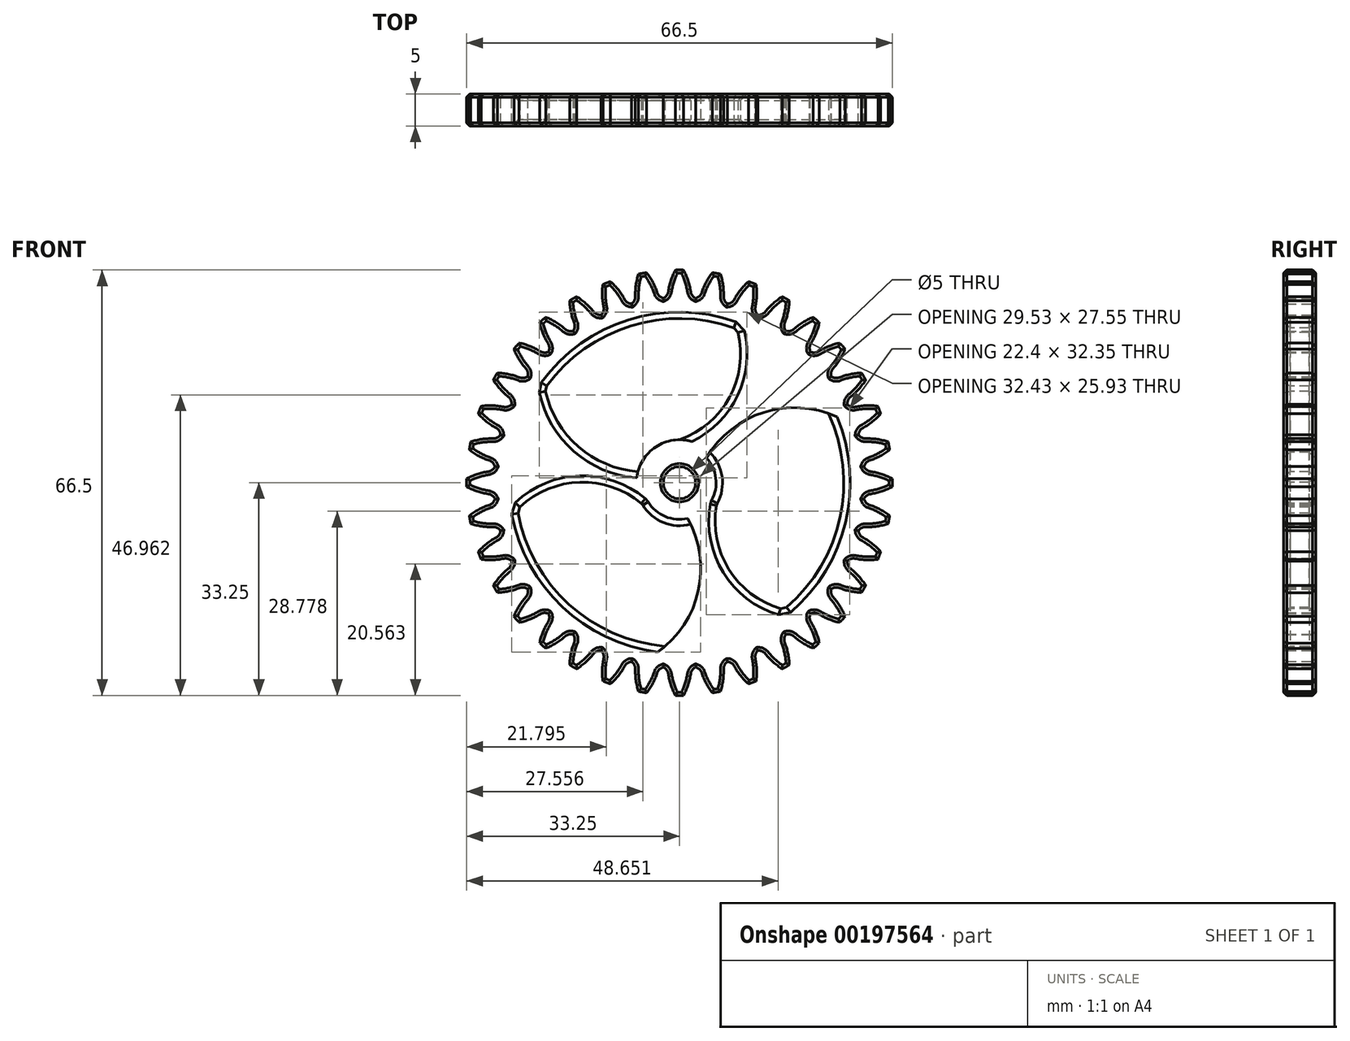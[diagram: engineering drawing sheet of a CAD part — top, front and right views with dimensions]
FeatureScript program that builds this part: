
annotation { "Feature Type Name" : "Feature", "Feature Type Description" : "" }
export const myFeature = defineFeature(function(context is Context, id is Id, definition is map)
    precondition{}
    {
        {
            var Q0;
            Q0=qCreatedBy(makeId("Front.planeOp"),FACE);
            var sketch = newSketch(context, id + "F0", { "sketchPlane" : qUnion([Q0])});
            skCircle(sketch, "E0", {"center": v(0, 0) * mm, "radius": 31.5 * mm, "construction": true});
            skCircle(sketch, "E1", {"center": v(0, 0) * mm, "radius": 29.6 * mm, "construction": true});
            skLineSegment(sketch, "E2", {"start": v(0, 0) * mm, "end": v(12.73, 40.38) * mm, "construction": true});
            skLineSegment(sketch, "E3", {"start": v(0, 0) * mm, "end": v(-1.92, 44) * mm, "construction": true});
            skLineSegment(sketch, "E4", {"start": v(0, 0) * mm, "end": v(0, 61.73) * mm, "construction": true});
            skArc(sketch, "E5", {"start": v(-0.64, 33.24) * mm, "mid": v(-1.33, 31.6) * mm, "end": v(-1.75, 29.87) * mm});
            skArc(sketch, "E6", {"start": v(0, 33.25) * mm, "mid": v(-0.32, 33.25) * mm, "end": v(-0.64, 33.24) * mm});
            skArc(sketch, "E7.MirrorCS", {"start": v(0, 33.25) * mm, "mid": v(0.32, 33.25) * mm, "end": v(0.64, 33.24) * mm});
            skArc(sketch, "E8.MirrorCS", {"start": v(0.64, 33.24) * mm, "mid": v(1.33, 31.6) * mm, "end": v(1.75, 29.87) * mm});
            skArc(sketch, "E9.filletArc", {"start": v(1.75, 29.87) * mm, "mid": v(2, 29.26) * mm, "end": v(2.52, 28.84) * mm});
            skArc(sketch, "E10.MirrorCS", {"start": v(-1.75, 29.87) * mm, "mid": v(-2, 29.26) * mm, "end": v(-2.52, 28.84) * mm});
            skArc(sketch, "E11.1.0", {"start": v(-5.77, 32.74) * mm, "mid": v(-6.09, 32.69) * mm, "end": v(-6.4, 32.63) * mm});
            skArc(sketch, "E11.1.1", {"start": v(-5.77, 32.74) * mm, "mid": v(-5.46, 32.8) * mm, "end": v(-5.15, 32.85) * mm});
            skArc(sketch, "E11.1.2", {"start": v(-5.15, 32.85) * mm, "mid": v(-4.18, 31.36) * mm, "end": v(-3.47, 29.72) * mm});
            skArc(sketch, "E11.1.3", {"start": v(-6.9, 29.12) * mm, "mid": v(-7.05, 28.47) * mm, "end": v(-7.5, 27.97) * mm});
            skArc(sketch, "E11.1.4", {"start": v(-6.4, 32.63) * mm, "mid": v(-6.8, 30.9) * mm, "end": v(-6.9, 29.12) * mm});
            skArc(sketch, "E11.1.5", {"start": v(-3.47, 29.72) * mm, "mid": v(-3.1, 29.16) * mm, "end": v(-2.52, 28.84) * mm});
            skArc(sketch, "E11.2.0", {"start": v(-11.37, 31.24) * mm, "mid": v(-11.67, 31.13) * mm, "end": v(-11.97, 31.02) * mm});
            skArc(sketch, "E11.2.1", {"start": v(-11.37, 31.24) * mm, "mid": v(-11.07, 31.35) * mm, "end": v(-10.77, 31.46) * mm});
            skArc(sketch, "E11.2.2", {"start": v(-10.77, 31.46) * mm, "mid": v(-9.56, 30.15) * mm, "end": v(-8.58, 28.67) * mm});
            skArc(sketch, "E11.2.3", {"start": v(-11.86, 27.48) * mm, "mid": v(-11.9, 26.8) * mm, "end": v(-12.24, 26.24) * mm});
            skArc(sketch, "E11.2.4", {"start": v(-11.97, 31.02) * mm, "mid": v(-12.06, 29.24) * mm, "end": v(-11.86, 27.48) * mm});
            skArc(sketch, "E11.2.5", {"start": v(-8.58, 28.67) * mm, "mid": v(-8.12, 28.18) * mm, "end": v(-7.5, 27.97) * mm});
            skArc(sketch, "E11.3.0", {"start": v(-16.63, 28.8) * mm, "mid": v(-16.9, 28.63) * mm, "end": v(-17.17, 28.47) * mm});
            skArc(sketch, "E11.3.1", {"start": v(-16.62, 28.8) * mm, "mid": v(-16.35, 28.95) * mm, "end": v(-16.07, 29.1) * mm});
            skArc(sketch, "E11.3.2", {"start": v(-16.07, 29.1) * mm, "mid": v(-14.65, 28.04) * mm, "end": v(-13.43, 26.74) * mm});
            skArc(sketch, "E11.3.3", {"start": v(-16.45, 25) * mm, "mid": v(-16.37, 24.34) * mm, "end": v(-16.6, 23.72) * mm});
            skArc(sketch, "E11.3.4", {"start": v(-17.17, 28.47) * mm, "mid": v(-16.95, 26.7) * mm, "end": v(-16.45, 25) * mm});
            skArc(sketch, "E11.3.5", {"start": v(-13.43, 26.74) * mm, "mid": v(-12.9, 26.34) * mm, "end": v(-12.24, 26.24) * mm});
            skArc(sketch, "E11.4.0", {"start": v(-21.37, 25.47) * mm, "mid": v(-21.62, 25.27) * mm, "end": v(-21.86, 25.06) * mm});
            skArc(sketch, "E11.4.1", {"start": v(-21.37, 25.47) * mm, "mid": v(-21.13, 25.67) * mm, "end": v(-20.88, 25.88) * mm});
            skArc(sketch, "E11.4.2", {"start": v(-20.88, 25.88) * mm, "mid": v(-19.3, 25.07) * mm, "end": v(-17.87, 24) * mm});
            skArc(sketch, "E11.4.3", {"start": v(-20.54, 21.76) * mm, "mid": v(-20.34, 21.13) * mm, "end": v(-20.47, 20.47) * mm});
            skArc(sketch, "E11.4.4", {"start": v(-21.86, 25.06) * mm, "mid": v(-21.33, 23.36) * mm, "end": v(-20.54, 21.76) * mm});
            skArc(sketch, "E11.4.5", {"start": v(-17.87, 24) * mm, "mid": v(-17.27, 23.7) * mm, "end": v(-16.6, 23.72) * mm});
            skArc(sketch, "E11.5.0", {"start": v(-25.47, 21.37) * mm, "mid": v(-25.67, 21.13) * mm, "end": v(-25.88, 20.88) * mm});
            skArc(sketch, "E11.5.1", {"start": v(-25.47, 21.37) * mm, "mid": v(-25.27, 21.62) * mm, "end": v(-25.06, 21.86) * mm});
            skArc(sketch, "E11.5.2", {"start": v(-25.06, 21.86) * mm, "mid": v(-23.36, 21.33) * mm, "end": v(-21.76, 20.54) * mm});
            skArc(sketch, "E11.5.3", {"start": v(-24, 17.87) * mm, "mid": v(-23.7, 17.27) * mm, "end": v(-23.72, 16.6) * mm});
            skArc(sketch, "E11.5.4", {"start": v(-25.88, 20.88) * mm, "mid": v(-25.07, 19.3) * mm, "end": v(-24, 17.87) * mm});
            skArc(sketch, "E11.5.5", {"start": v(-21.76, 20.54) * mm, "mid": v(-21.13, 20.34) * mm, "end": v(-20.47, 20.47) * mm});
            skArc(sketch, "E11.6.0", {"start": v(-28.8, 16.62) * mm, "mid": v(-28.95, 16.35) * mm, "end": v(-29.1, 16.07) * mm});
            skArc(sketch, "E11.6.1", {"start": v(-28.8, 16.63) * mm, "mid": v(-28.63, 16.9) * mm, "end": v(-28.47, 17.17) * mm});
            skArc(sketch, "E11.6.2", {"start": v(-28.47, 17.17) * mm, "mid": v(-26.7, 16.95) * mm, "end": v(-25, 16.45) * mm});
            skArc(sketch, "E11.6.3", {"start": v(-26.74, 13.43) * mm, "mid": v(-26.34, 12.9) * mm, "end": v(-26.24, 12.24) * mm});
            skArc(sketch, "E11.6.4", {"start": v(-29.1, 16.07) * mm, "mid": v(-28.04, 14.65) * mm, "end": v(-26.74, 13.43) * mm});
            skArc(sketch, "E11.6.5", {"start": v(-25, 16.45) * mm, "mid": v(-24.34, 16.37) * mm, "end": v(-23.72, 16.6) * mm});
            skArc(sketch, "E11.7.0", {"start": v(-31.24, 11.37) * mm, "mid": v(-31.35, 11.07) * mm, "end": v(-31.46, 10.77) * mm});
            skArc(sketch, "E11.7.1", {"start": v(-31.24, 11.37) * mm, "mid": v(-31.13, 11.67) * mm, "end": v(-31.02, 11.97) * mm});
            skArc(sketch, "E11.7.2", {"start": v(-31.02, 11.97) * mm, "mid": v(-29.24, 12.06) * mm, "end": v(-27.48, 11.86) * mm});
            skArc(sketch, "E11.7.3", {"start": v(-28.67, 8.58) * mm, "mid": v(-28.18, 8.12) * mm, "end": v(-27.97, 7.5) * mm});
            skArc(sketch, "E11.7.4", {"start": v(-31.46, 10.77) * mm, "mid": v(-30.15, 9.56) * mm, "end": v(-28.67, 8.58) * mm});
            skArc(sketch, "E11.7.5", {"start": v(-27.48, 11.86) * mm, "mid": v(-26.8, 11.9) * mm, "end": v(-26.24, 12.24) * mm});
            skArc(sketch, "E11.8.0", {"start": v(-32.74, 5.77) * mm, "mid": v(-32.8, 5.46) * mm, "end": v(-32.85, 5.15) * mm});
            skArc(sketch, "E11.8.1", {"start": v(-32.74, 5.77) * mm, "mid": v(-32.69, 6.09) * mm, "end": v(-32.63, 6.4) * mm});
            skArc(sketch, "E11.8.2", {"start": v(-32.63, 6.4) * mm, "mid": v(-30.9, 6.8) * mm, "end": v(-29.12, 6.9) * mm});
            skArc(sketch, "E11.8.3", {"start": v(-29.72, 3.47) * mm, "mid": v(-29.16, 3.1) * mm, "end": v(-28.84, 2.52) * mm});
            skArc(sketch, "E11.8.4", {"start": v(-32.85, 5.15) * mm, "mid": v(-31.36, 4.18) * mm, "end": v(-29.72, 3.47) * mm});
            skArc(sketch, "E11.8.5", {"start": v(-29.12, 6.9) * mm, "mid": v(-28.47, 7.05) * mm, "end": v(-27.97, 7.5) * mm});
            skArc(sketch, "E11.9.0", {"start": v(-33.25, 0) * mm, "mid": v(-33.25, -0.32) * mm, "end": v(-33.24, -0.64) * mm});
            skArc(sketch, "E11.9.1", {"start": v(-33.25, 0) * mm, "mid": v(-33.25, 0.32) * mm, "end": v(-33.24, 0.64) * mm});
            skArc(sketch, "E11.9.2", {"start": v(-33.24, 0.64) * mm, "mid": v(-31.6, 1.33) * mm, "end": v(-29.87, 1.75) * mm});
            skArc(sketch, "E11.9.3", {"start": v(-29.87, -1.75) * mm, "mid": v(-29.26, -2) * mm, "end": v(-28.84, -2.52) * mm});
            skArc(sketch, "E11.9.4", {"start": v(-33.24, -0.64) * mm, "mid": v(-31.6, -1.33) * mm, "end": v(-29.87, -1.75) * mm});
            skArc(sketch, "E11.9.5", {"start": v(-29.87, 1.75) * mm, "mid": v(-29.26, 2) * mm, "end": v(-28.84, 2.52) * mm});
            skArc(sketch, "E11.10.0", {"start": v(-32.74, -5.77) * mm, "mid": v(-32.69, -6.09) * mm, "end": v(-32.63, -6.4) * mm});
            skArc(sketch, "E11.10.1", {"start": v(-32.74, -5.77) * mm, "mid": v(-32.8, -5.46) * mm, "end": v(-32.85, -5.15) * mm});
            skArc(sketch, "E11.10.2", {"start": v(-32.85, -5.15) * mm, "mid": v(-31.36, -4.18) * mm, "end": v(-29.72, -3.47) * mm});
            skArc(sketch, "E11.10.3", {"start": v(-29.12, -6.9) * mm, "mid": v(-28.47, -7.05) * mm, "end": v(-27.97, -7.5) * mm});
            skArc(sketch, "E11.10.4", {"start": v(-32.63, -6.4) * mm, "mid": v(-30.9, -6.8) * mm, "end": v(-29.12, -6.9) * mm});
            skArc(sketch, "E11.10.5", {"start": v(-29.72, -3.47) * mm, "mid": v(-29.16, -3.1) * mm, "end": v(-28.84, -2.52) * mm});
            skArc(sketch, "E11.11.0", {"start": v(-31.24, -11.37) * mm, "mid": v(-31.13, -11.67) * mm, "end": v(-31.02, -11.97) * mm});
            skArc(sketch, "E11.11.1", {"start": v(-31.24, -11.37) * mm, "mid": v(-31.35, -11.07) * mm, "end": v(-31.46, -10.77) * mm});
            skArc(sketch, "E11.11.2", {"start": v(-31.46, -10.77) * mm, "mid": v(-30.15, -9.56) * mm, "end": v(-28.67, -8.58) * mm});
            skArc(sketch, "E11.11.3", {"start": v(-27.48, -11.86) * mm, "mid": v(-26.8, -11.9) * mm, "end": v(-26.24, -12.24) * mm});
            skArc(sketch, "E11.11.4", {"start": v(-31.02, -11.97) * mm, "mid": v(-29.24, -12.06) * mm, "end": v(-27.48, -11.86) * mm});
            skArc(sketch, "E11.11.5", {"start": v(-28.67, -8.58) * mm, "mid": v(-28.18, -8.12) * mm, "end": v(-27.97, -7.5) * mm});
            skArc(sketch, "E11.12.0", {"start": v(-28.8, -16.62) * mm, "mid": v(-28.63, -16.9) * mm, "end": v(-28.47, -17.17) * mm});
            skArc(sketch, "E11.12.1", {"start": v(-28.8, -16.62) * mm, "mid": v(-28.95, -16.35) * mm, "end": v(-29.1, -16.07) * mm});
            skArc(sketch, "E11.12.2", {"start": v(-29.1, -16.07) * mm, "mid": v(-28.04, -14.65) * mm, "end": v(-26.74, -13.43) * mm});
            skArc(sketch, "E11.12.3", {"start": v(-25, -16.45) * mm, "mid": v(-24.34, -16.37) * mm, "end": v(-23.72, -16.6) * mm});
            skArc(sketch, "E11.12.4", {"start": v(-28.47, -17.17) * mm, "mid": v(-26.7, -16.95) * mm, "end": v(-25, -16.45) * mm});
            skArc(sketch, "E11.12.5", {"start": v(-26.74, -13.43) * mm, "mid": v(-26.34, -12.9) * mm, "end": v(-26.24, -12.24) * mm});
            skArc(sketch, "E11.13.0", {"start": v(-25.47, -21.37) * mm, "mid": v(-25.27, -21.62) * mm, "end": v(-25.06, -21.86) * mm});
            skArc(sketch, "E11.13.1", {"start": v(-25.47, -21.37) * mm, "mid": v(-25.67, -21.13) * mm, "end": v(-25.88, -20.88) * mm});
            skArc(sketch, "E11.13.2", {"start": v(-25.88, -20.88) * mm, "mid": v(-25.07, -19.3) * mm, "end": v(-24, -17.87) * mm});
            skArc(sketch, "E11.13.3", {"start": v(-21.76, -20.54) * mm, "mid": v(-21.13, -20.34) * mm, "end": v(-20.47, -20.47) * mm});
            skArc(sketch, "E11.13.4", {"start": v(-25.06, -21.86) * mm, "mid": v(-23.36, -21.33) * mm, "end": v(-21.76, -20.54) * mm});
            skArc(sketch, "E11.13.5", {"start": v(-24, -17.87) * mm, "mid": v(-23.7, -17.27) * mm, "end": v(-23.72, -16.6) * mm});
            skArc(sketch, "E11.14.0", {"start": v(-21.37, -25.47) * mm, "mid": v(-21.13, -25.67) * mm, "end": v(-20.88, -25.88) * mm});
            skArc(sketch, "E11.14.1", {"start": v(-21.37, -25.47) * mm, "mid": v(-21.62, -25.27) * mm, "end": v(-21.86, -25.06) * mm});
            skArc(sketch, "E11.14.2", {"start": v(-21.86, -25.06) * mm, "mid": v(-21.33, -23.36) * mm, "end": v(-20.54, -21.76) * mm});
            skArc(sketch, "E11.14.3", {"start": v(-17.87, -24) * mm, "mid": v(-17.27, -23.7) * mm, "end": v(-16.6, -23.72) * mm});
            skArc(sketch, "E11.14.4", {"start": v(-20.88, -25.88) * mm, "mid": v(-19.3, -25.07) * mm, "end": v(-17.87, -24) * mm});
            skArc(sketch, "E11.14.5", {"start": v(-20.54, -21.76) * mm, "mid": v(-20.34, -21.13) * mm, "end": v(-20.47, -20.47) * mm});
            skArc(sketch, "E11.15.0", {"start": v(-16.63, -28.8) * mm, "mid": v(-16.35, -28.95) * mm, "end": v(-16.07, -29.1) * mm});
            skArc(sketch, "E11.15.1", {"start": v(-16.63, -28.8) * mm, "mid": v(-16.9, -28.63) * mm, "end": v(-17.17, -28.47) * mm});
            skArc(sketch, "E11.15.2", {"start": v(-17.17, -28.47) * mm, "mid": v(-16.95, -26.7) * mm, "end": v(-16.45, -25) * mm});
            skArc(sketch, "E11.15.3", {"start": v(-13.43, -26.74) * mm, "mid": v(-12.9, -26.34) * mm, "end": v(-12.24, -26.24) * mm});
            skArc(sketch, "E11.15.4", {"start": v(-16.07, -29.1) * mm, "mid": v(-14.65, -28.04) * mm, "end": v(-13.43, -26.74) * mm});
            skArc(sketch, "E11.15.5", {"start": v(-16.45, -25) * mm, "mid": v(-16.37, -24.34) * mm, "end": v(-16.6, -23.72) * mm});
            skArc(sketch, "E11.16.0", {"start": v(-11.37, -31.24) * mm, "mid": v(-11.07, -31.35) * mm, "end": v(-10.77, -31.46) * mm});
            skArc(sketch, "E11.16.1", {"start": v(-11.37, -31.24) * mm, "mid": v(-11.67, -31.13) * mm, "end": v(-11.97, -31.02) * mm});
            skArc(sketch, "E11.16.2", {"start": v(-11.97, -31.02) * mm, "mid": v(-12.06, -29.24) * mm, "end": v(-11.86, -27.48) * mm});
            skArc(sketch, "E11.16.3", {"start": v(-8.58, -28.67) * mm, "mid": v(-8.12, -28.18) * mm, "end": v(-7.5, -27.97) * mm});
            skArc(sketch, "E11.16.4", {"start": v(-10.77, -31.46) * mm, "mid": v(-9.56, -30.15) * mm, "end": v(-8.58, -28.67) * mm});
            skArc(sketch, "E11.16.5", {"start": v(-11.86, -27.48) * mm, "mid": v(-11.9, -26.8) * mm, "end": v(-12.24, -26.24) * mm});
            skArc(sketch, "E11.17.0", {"start": v(-5.77, -32.74) * mm, "mid": v(-5.46, -32.8) * mm, "end": v(-5.15, -32.85) * mm});
            skArc(sketch, "E11.17.1", {"start": v(-5.77, -32.74) * mm, "mid": v(-6.09, -32.69) * mm, "end": v(-6.4, -32.63) * mm});
            skArc(sketch, "E11.17.2", {"start": v(-6.4, -32.63) * mm, "mid": v(-6.8, -30.9) * mm, "end": v(-6.9, -29.12) * mm});
            skArc(sketch, "E11.17.3", {"start": v(-3.47, -29.72) * mm, "mid": v(-3.1, -29.16) * mm, "end": v(-2.52, -28.84) * mm});
            skArc(sketch, "E11.17.4", {"start": v(-5.15, -32.85) * mm, "mid": v(-4.18, -31.36) * mm, "end": v(-3.47, -29.72) * mm});
            skArc(sketch, "E11.17.5", {"start": v(-6.9, -29.12) * mm, "mid": v(-7.05, -28.47) * mm, "end": v(-7.5, -27.97) * mm});
            skArc(sketch, "E11.18.0", {"start": v(0, -33.25) * mm, "mid": v(0.32, -33.25) * mm, "end": v(0.64, -33.24) * mm});
            skArc(sketch, "E11.18.1", {"start": v(0, -33.25) * mm, "mid": v(-0.32, -33.25) * mm, "end": v(-0.64, -33.24) * mm});
            skArc(sketch, "E11.18.2", {"start": v(-0.64, -33.24) * mm, "mid": v(-1.33, -31.6) * mm, "end": v(-1.75, -29.87) * mm});
            skArc(sketch, "E11.18.3", {"start": v(1.75, -29.87) * mm, "mid": v(2, -29.26) * mm, "end": v(2.52, -28.84) * mm});
            skArc(sketch, "E11.18.4", {"start": v(0.64, -33.24) * mm, "mid": v(1.33, -31.6) * mm, "end": v(1.75, -29.87) * mm});
            skArc(sketch, "E11.18.5", {"start": v(-1.75, -29.87) * mm, "mid": v(-2, -29.26) * mm, "end": v(-2.52, -28.84) * mm});
            skArc(sketch, "E11.19.0", {"start": v(5.77, -32.74) * mm, "mid": v(6.09, -32.69) * mm, "end": v(6.4, -32.63) * mm});
            skArc(sketch, "E11.19.1", {"start": v(5.77, -32.74) * mm, "mid": v(5.46, -32.8) * mm, "end": v(5.15, -32.85) * mm});
            skArc(sketch, "E11.19.2", {"start": v(5.15, -32.85) * mm, "mid": v(4.18, -31.36) * mm, "end": v(3.47, -29.72) * mm});
            skArc(sketch, "E11.19.3", {"start": v(6.9, -29.12) * mm, "mid": v(7.05, -28.47) * mm, "end": v(7.5, -27.97) * mm});
            skArc(sketch, "E11.19.4", {"start": v(6.4, -32.63) * mm, "mid": v(6.8, -30.9) * mm, "end": v(6.9, -29.12) * mm});
            skArc(sketch, "E11.19.5", {"start": v(3.47, -29.72) * mm, "mid": v(3.1, -29.16) * mm, "end": v(2.52, -28.84) * mm});
            skArc(sketch, "E11.20.0", {"start": v(11.37, -31.24) * mm, "mid": v(11.67, -31.13) * mm, "end": v(11.97, -31.02) * mm});
            skArc(sketch, "E11.20.1", {"start": v(11.37, -31.24) * mm, "mid": v(11.07, -31.35) * mm, "end": v(10.77, -31.46) * mm});
            skArc(sketch, "E11.20.2", {"start": v(10.77, -31.46) * mm, "mid": v(9.56, -30.15) * mm, "end": v(8.58, -28.67) * mm});
            skArc(sketch, "E11.20.3", {"start": v(11.86, -27.48) * mm, "mid": v(11.9, -26.8) * mm, "end": v(12.24, -26.24) * mm});
            skArc(sketch, "E11.20.4", {"start": v(11.97, -31.02) * mm, "mid": v(12.06, -29.24) * mm, "end": v(11.86, -27.48) * mm});
            skArc(sketch, "E11.20.5", {"start": v(8.58, -28.67) * mm, "mid": v(8.12, -28.18) * mm, "end": v(7.5, -27.97) * mm});
            skArc(sketch, "E11.21.0", {"start": v(16.63, -28.8) * mm, "mid": v(16.9, -28.63) * mm, "end": v(17.17, -28.47) * mm});
            skArc(sketch, "E11.21.1", {"start": v(16.62, -28.8) * mm, "mid": v(16.35, -28.95) * mm, "end": v(16.07, -29.1) * mm});
            skArc(sketch, "E11.21.2", {"start": v(16.07, -29.1) * mm, "mid": v(14.65, -28.04) * mm, "end": v(13.43, -26.74) * mm});
            skArc(sketch, "E11.21.3", {"start": v(16.45, -25) * mm, "mid": v(16.37, -24.34) * mm, "end": v(16.6, -23.72) * mm});
            skArc(sketch, "E11.21.4", {"start": v(17.17, -28.47) * mm, "mid": v(16.95, -26.7) * mm, "end": v(16.45, -25) * mm});
            skArc(sketch, "E11.21.5", {"start": v(13.43, -26.74) * mm, "mid": v(12.9, -26.34) * mm, "end": v(12.24, -26.24) * mm});
            skArc(sketch, "E11.22.0", {"start": v(21.37, -25.47) * mm, "mid": v(21.62, -25.27) * mm, "end": v(21.86, -25.06) * mm});
            skArc(sketch, "E11.22.1", {"start": v(21.37, -25.47) * mm, "mid": v(21.13, -25.67) * mm, "end": v(20.88, -25.88) * mm});
            skArc(sketch, "E11.22.2", {"start": v(20.88, -25.88) * mm, "mid": v(19.3, -25.07) * mm, "end": v(17.87, -24) * mm});
            skArc(sketch, "E11.22.3", {"start": v(20.54, -21.76) * mm, "mid": v(20.34, -21.13) * mm, "end": v(20.47, -20.47) * mm});
            skArc(sketch, "E11.22.4", {"start": v(21.86, -25.06) * mm, "mid": v(21.33, -23.36) * mm, "end": v(20.54, -21.76) * mm});
            skArc(sketch, "E11.22.5", {"start": v(17.87, -24) * mm, "mid": v(17.27, -23.7) * mm, "end": v(16.6, -23.72) * mm});
            skArc(sketch, "E11.23.0", {"start": v(25.47, -21.37) * mm, "mid": v(25.67, -21.13) * mm, "end": v(25.88, -20.88) * mm});
            skArc(sketch, "E11.23.1", {"start": v(25.47, -21.37) * mm, "mid": v(25.27, -21.62) * mm, "end": v(25.06, -21.86) * mm});
            skArc(sketch, "E11.23.2", {"start": v(25.06, -21.86) * mm, "mid": v(23.36, -21.33) * mm, "end": v(21.76, -20.54) * mm});
            skArc(sketch, "E11.23.3", {"start": v(24, -17.87) * mm, "mid": v(23.7, -17.27) * mm, "end": v(23.72, -16.6) * mm});
            skArc(sketch, "E11.23.4", {"start": v(25.88, -20.88) * mm, "mid": v(25.07, -19.3) * mm, "end": v(24, -17.87) * mm});
            skArc(sketch, "E11.23.5", {"start": v(21.76, -20.54) * mm, "mid": v(21.13, -20.34) * mm, "end": v(20.47, -20.47) * mm});
            skArc(sketch, "E11.24.0", {"start": v(28.8, -16.63) * mm, "mid": v(28.95, -16.35) * mm, "end": v(29.1, -16.07) * mm});
            skArc(sketch, "E11.24.1", {"start": v(28.8, -16.63) * mm, "mid": v(28.63, -16.9) * mm, "end": v(28.47, -17.17) * mm});
            skArc(sketch, "E11.24.2", {"start": v(28.47, -17.17) * mm, "mid": v(26.7, -16.95) * mm, "end": v(25, -16.45) * mm});
            skArc(sketch, "E11.24.3", {"start": v(26.74, -13.43) * mm, "mid": v(26.34, -12.9) * mm, "end": v(26.24, -12.24) * mm});
            skArc(sketch, "E11.24.4", {"start": v(29.1, -16.07) * mm, "mid": v(28.04, -14.65) * mm, "end": v(26.74, -13.43) * mm});
            skArc(sketch, "E11.24.5", {"start": v(25, -16.45) * mm, "mid": v(24.34, -16.37) * mm, "end": v(23.72, -16.6) * mm});
            skArc(sketch, "E11.25.0", {"start": v(31.24, -11.37) * mm, "mid": v(31.35, -11.07) * mm, "end": v(31.46, -10.77) * mm});
            skArc(sketch, "E11.25.1", {"start": v(31.24, -11.37) * mm, "mid": v(31.13, -11.67) * mm, "end": v(31.02, -11.97) * mm});
            skArc(sketch, "E11.25.2", {"start": v(31.02, -11.97) * mm, "mid": v(29.24, -12.06) * mm, "end": v(27.48, -11.86) * mm});
            skArc(sketch, "E11.25.3", {"start": v(28.67, -8.58) * mm, "mid": v(28.18, -8.12) * mm, "end": v(27.97, -7.5) * mm});
            skArc(sketch, "E11.25.4", {"start": v(31.46, -10.77) * mm, "mid": v(30.15, -9.56) * mm, "end": v(28.67, -8.58) * mm});
            skArc(sketch, "E11.25.5", {"start": v(27.48, -11.86) * mm, "mid": v(26.8, -11.9) * mm, "end": v(26.24, -12.24) * mm});
            skArc(sketch, "E11.26.0", {"start": v(32.74, -5.77) * mm, "mid": v(32.8, -5.46) * mm, "end": v(32.85, -5.15) * mm});
            skArc(sketch, "E11.26.1", {"start": v(32.74, -5.77) * mm, "mid": v(32.69, -6.09) * mm, "end": v(32.63, -6.4) * mm});
            skArc(sketch, "E11.26.2", {"start": v(32.63, -6.4) * mm, "mid": v(30.9, -6.8) * mm, "end": v(29.12, -6.9) * mm});
            skArc(sketch, "E11.26.3", {"start": v(29.72, -3.47) * mm, "mid": v(29.16, -3.1) * mm, "end": v(28.84, -2.52) * mm});
            skArc(sketch, "E11.26.4", {"start": v(32.85, -5.15) * mm, "mid": v(31.36, -4.18) * mm, "end": v(29.72, -3.47) * mm});
            skArc(sketch, "E11.26.5", {"start": v(29.12, -6.9) * mm, "mid": v(28.47, -7.05) * mm, "end": v(27.97, -7.5) * mm});
            skArc(sketch, "E11.27.0", {"start": v(33.25, 0) * mm, "mid": v(33.25, 0.32) * mm, "end": v(33.24, 0.64) * mm});
            skArc(sketch, "E11.27.1", {"start": v(33.25, 0) * mm, "mid": v(33.25, -0.32) * mm, "end": v(33.24, -0.64) * mm});
            skArc(sketch, "E11.27.2", {"start": v(33.24, -0.64) * mm, "mid": v(31.6, -1.33) * mm, "end": v(29.87, -1.75) * mm});
            skArc(sketch, "E11.27.3", {"start": v(29.87, 1.75) * mm, "mid": v(29.26, 2) * mm, "end": v(28.84, 2.52) * mm});
            skArc(sketch, "E11.27.4", {"start": v(33.24, 0.64) * mm, "mid": v(31.6, 1.33) * mm, "end": v(29.87, 1.75) * mm});
            skArc(sketch, "E11.27.5", {"start": v(29.87, -1.75) * mm, "mid": v(29.26, -2) * mm, "end": v(28.84, -2.52) * mm});
            skArc(sketch, "E11.28.0", {"start": v(32.74, 5.77) * mm, "mid": v(32.69, 6.09) * mm, "end": v(32.63, 6.4) * mm});
            skArc(sketch, "E11.28.1", {"start": v(32.74, 5.77) * mm, "mid": v(32.8, 5.46) * mm, "end": v(32.85, 5.15) * mm});
            skArc(sketch, "E11.28.2", {"start": v(32.85, 5.15) * mm, "mid": v(31.36, 4.18) * mm, "end": v(29.72, 3.47) * mm});
            skArc(sketch, "E11.28.3", {"start": v(29.12, 6.9) * mm, "mid": v(28.47, 7.05) * mm, "end": v(27.97, 7.5) * mm});
            skArc(sketch, "E11.28.4", {"start": v(32.63, 6.4) * mm, "mid": v(30.9, 6.8) * mm, "end": v(29.12, 6.9) * mm});
            skArc(sketch, "E11.28.5", {"start": v(29.72, 3.47) * mm, "mid": v(29.16, 3.1) * mm, "end": v(28.84, 2.52) * mm});
            skArc(sketch, "E11.29.0", {"start": v(31.24, 11.37) * mm, "mid": v(31.13, 11.67) * mm, "end": v(31.02, 11.97) * mm});
            skArc(sketch, "E11.29.1", {"start": v(31.24, 11.37) * mm, "mid": v(31.35, 11.07) * mm, "end": v(31.46, 10.77) * mm});
            skArc(sketch, "E11.29.2", {"start": v(31.46, 10.77) * mm, "mid": v(30.15, 9.56) * mm, "end": v(28.67, 8.58) * mm});
            skArc(sketch, "E11.29.3", {"start": v(27.48, 11.86) * mm, "mid": v(26.8, 11.9) * mm, "end": v(26.24, 12.24) * mm});
            skArc(sketch, "E11.29.4", {"start": v(31.02, 11.97) * mm, "mid": v(29.24, 12.06) * mm, "end": v(27.48, 11.86) * mm});
            skArc(sketch, "E11.29.5", {"start": v(28.67, 8.58) * mm, "mid": v(28.18, 8.12) * mm, "end": v(27.97, 7.5) * mm});
            skArc(sketch, "E11.30.0", {"start": v(28.8, 16.62) * mm, "mid": v(28.63, 16.9) * mm, "end": v(28.47, 17.17) * mm});
            skArc(sketch, "E11.30.1", {"start": v(28.8, 16.62) * mm, "mid": v(28.95, 16.35) * mm, "end": v(29.1, 16.07) * mm});
            skArc(sketch, "E11.30.2", {"start": v(29.1, 16.07) * mm, "mid": v(28.04, 14.65) * mm, "end": v(26.74, 13.43) * mm});
            skArc(sketch, "E11.30.3", {"start": v(25, 16.45) * mm, "mid": v(24.34, 16.37) * mm, "end": v(23.72, 16.6) * mm});
            skArc(sketch, "E11.30.4", {"start": v(28.47, 17.17) * mm, "mid": v(26.7, 16.95) * mm, "end": v(25, 16.45) * mm});
            skArc(sketch, "E11.30.5", {"start": v(26.74, 13.43) * mm, "mid": v(26.34, 12.9) * mm, "end": v(26.24, 12.24) * mm});
            skArc(sketch, "E11.31.0", {"start": v(25.47, 21.37) * mm, "mid": v(25.27, 21.62) * mm, "end": v(25.06, 21.86) * mm});
            skArc(sketch, "E11.31.1", {"start": v(25.47, 21.37) * mm, "mid": v(25.67, 21.13) * mm, "end": v(25.88, 20.88) * mm});
            skArc(sketch, "E11.31.2", {"start": v(25.88, 20.88) * mm, "mid": v(25.07, 19.3) * mm, "end": v(24, 17.87) * mm});
            skArc(sketch, "E11.31.3", {"start": v(21.76, 20.54) * mm, "mid": v(21.13, 20.34) * mm, "end": v(20.47, 20.47) * mm});
            skArc(sketch, "E11.31.4", {"start": v(25.06, 21.86) * mm, "mid": v(23.36, 21.33) * mm, "end": v(21.76, 20.54) * mm});
            skArc(sketch, "E11.31.5", {"start": v(24, 17.87) * mm, "mid": v(23.7, 17.27) * mm, "end": v(23.72, 16.6) * mm});
            skArc(sketch, "E11.32.0", {"start": v(21.37, 25.47) * mm, "mid": v(21.13, 25.67) * mm, "end": v(20.88, 25.88) * mm});
            skArc(sketch, "E11.32.1", {"start": v(21.37, 25.47) * mm, "mid": v(21.62, 25.27) * mm, "end": v(21.86, 25.06) * mm});
            skArc(sketch, "E11.32.2", {"start": v(21.86, 25.06) * mm, "mid": v(21.33, 23.36) * mm, "end": v(20.54, 21.76) * mm});
            skArc(sketch, "E11.32.3", {"start": v(17.87, 24) * mm, "mid": v(17.27, 23.7) * mm, "end": v(16.6, 23.72) * mm});
            skArc(sketch, "E11.32.4", {"start": v(20.88, 25.88) * mm, "mid": v(19.3, 25.07) * mm, "end": v(17.87, 24) * mm});
            skArc(sketch, "E11.32.5", {"start": v(20.54, 21.76) * mm, "mid": v(20.34, 21.13) * mm, "end": v(20.47, 20.47) * mm});
            skArc(sketch, "E11.33.0", {"start": v(16.62, 28.8) * mm, "mid": v(16.35, 28.95) * mm, "end": v(16.07, 29.1) * mm});
            skArc(sketch, "E11.33.1", {"start": v(16.62, 28.8) * mm, "mid": v(16.9, 28.63) * mm, "end": v(17.17, 28.47) * mm});
            skArc(sketch, "E11.33.2", {"start": v(17.17, 28.47) * mm, "mid": v(16.95, 26.7) * mm, "end": v(16.45, 25) * mm});
            skArc(sketch, "E11.33.3", {"start": v(13.43, 26.74) * mm, "mid": v(12.9, 26.34) * mm, "end": v(12.24, 26.24) * mm});
            skArc(sketch, "E11.33.4", {"start": v(16.07, 29.1) * mm, "mid": v(14.65, 28.04) * mm, "end": v(13.43, 26.74) * mm});
            skArc(sketch, "E11.33.5", {"start": v(16.45, 25) * mm, "mid": v(16.37, 24.34) * mm, "end": v(16.6, 23.72) * mm});
            skArc(sketch, "E11.34.0", {"start": v(11.37, 31.24) * mm, "mid": v(11.07, 31.35) * mm, "end": v(10.77, 31.46) * mm});
            skArc(sketch, "E11.34.1", {"start": v(11.37, 31.24) * mm, "mid": v(11.67, 31.13) * mm, "end": v(11.97, 31.02) * mm});
            skArc(sketch, "E11.34.2", {"start": v(11.97, 31.02) * mm, "mid": v(12.06, 29.24) * mm, "end": v(11.86, 27.48) * mm});
            skArc(sketch, "E11.34.3", {"start": v(8.58, 28.67) * mm, "mid": v(8.12, 28.18) * mm, "end": v(7.5, 27.97) * mm});
            skArc(sketch, "E11.34.4", {"start": v(10.77, 31.46) * mm, "mid": v(9.56, 30.15) * mm, "end": v(8.58, 28.67) * mm});
            skArc(sketch, "E11.34.5", {"start": v(11.86, 27.48) * mm, "mid": v(11.9, 26.8) * mm, "end": v(12.24, 26.24) * mm});
            skArc(sketch, "E11.35.0", {"start": v(5.77, 32.74) * mm, "mid": v(5.46, 32.8) * mm, "end": v(5.15, 32.85) * mm});
            skArc(sketch, "E11.35.1", {"start": v(5.77, 32.74) * mm, "mid": v(6.09, 32.69) * mm, "end": v(6.4, 32.63) * mm});
            skArc(sketch, "E11.35.2", {"start": v(6.4, 32.63) * mm, "mid": v(6.8, 30.9) * mm, "end": v(6.9, 29.12) * mm});
            skArc(sketch, "E11.35.3", {"start": v(3.47, 29.72) * mm, "mid": v(3.1, 29.16) * mm, "end": v(2.52, 28.84) * mm});
            skArc(sketch, "E11.35.4", {"start": v(5.15, 32.85) * mm, "mid": v(4.18, 31.36) * mm, "end": v(3.47, 29.72) * mm});
            skArc(sketch, "E11.35.5", {"start": v(6.9, 29.12) * mm, "mid": v(7.05, 28.47) * mm, "end": v(7.5, 27.97) * mm});
            skCircle(sketch, "E12", {"center": v(0, 0) * mm, "radius": 2.5 * mm});
            skSolve(sketch);
        }
        {
            var Q0;
            Q0=makeQuery(id+"F0.imprint","IMPRINT",FACE,{"disambiguationData":[TD([[makeQuery(id+"F0.imprint","IMPRINT",EDGE,{"derivedFrom":sQuery(id+"F0.wireOp",EDGE,"E5")}),1.0]])]});
            extrude(context, id + "F1", {"entities" : qUnion([Q0]), "depth" : 5 * mm});
        }
        {
            var Q0;
            Q0=makeQuery(id+"F1.opExtrude","CAP_FACE",FACE,{"disambiguationData":[OSD([sQuery(id+"F0.wireOp",EDGE,"E5"),sQuery(id+"F0.wireOp",EDGE,"E6"),sQuery(id+"F0.wireOp",EDGE,"E7.MirrorCS"),sQuery(id+"F0.wireOp",EDGE,"E8.MirrorCS"),sQuery(id+"F0.wireOp",EDGE,"E9.filletArc"),sQuery(id+"F0.wireOp",EDGE,"E10.MirrorCS"),sQuery(id+"F0.wireOp",EDGE,"E11.1.0"),sQuery(id+"F0.wireOp",EDGE,"E11.1.1"),sQuery(id+"F0.wireOp",EDGE,"E11.1.2"),sQuery(id+"F0.wireOp",EDGE,"E11.1.3"),sQuery(id+"F0.wireOp",EDGE,"E11.1.4"),sQuery(id+"F0.wireOp",EDGE,"E11.1.5"),sQuery(id+"F0.wireOp",EDGE,"E11.2.0"),sQuery(id+"F0.wireOp",EDGE,"E11.2.1"),sQuery(id+"F0.wireOp",EDGE,"E11.2.2"),sQuery(id+"F0.wireOp",EDGE,"E11.2.3"),sQuery(id+"F0.wireOp",EDGE,"E11.2.4"),sQuery(id+"F0.wireOp",EDGE,"E11.2.5"),sQuery(id+"F0.wireOp",EDGE,"E11.3.0"),sQuery(id+"F0.wireOp",EDGE,"E11.3.1"),sQuery(id+"F0.wireOp",EDGE,"E11.3.2"),sQuery(id+"F0.wireOp",EDGE,"E11.3.3"),sQuery(id+"F0.wireOp",EDGE,"E11.3.4"),sQuery(id+"F0.wireOp",EDGE,"E11.3.5"),sQuery(id+"F0.wireOp",EDGE,"E11.4.0"),sQuery(id+"F0.wireOp",EDGE,"E11.4.1"),sQuery(id+"F0.wireOp",EDGE,"E11.4.2"),sQuery(id+"F0.wireOp",EDGE,"E11.4.3"),sQuery(id+"F0.wireOp",EDGE,"E11.4.4"),sQuery(id+"F0.wireOp",EDGE,"E11.4.5"),sQuery(id+"F0.wireOp",EDGE,"E11.5.0"),sQuery(id+"F0.wireOp",EDGE,"E11.5.1"),sQuery(id+"F0.wireOp",EDGE,"E11.5.2"),sQuery(id+"F0.wireOp",EDGE,"E11.5.3"),sQuery(id+"F0.wireOp",EDGE,"E11.5.4"),sQuery(id+"F0.wireOp",EDGE,"E11.5.5"),sQuery(id+"F0.wireOp",EDGE,"E11.6.0"),sQuery(id+"F0.wireOp",EDGE,"E11.6.1"),sQuery(id+"F0.wireOp",EDGE,"E11.6.2"),sQuery(id+"F0.wireOp",EDGE,"E11.6.3"),sQuery(id+"F0.wireOp",EDGE,"E11.6.4"),sQuery(id+"F0.wireOp",EDGE,"E11.6.5"),sQuery(id+"F0.wireOp",EDGE,"E11.7.0"),sQuery(id+"F0.wireOp",EDGE,"E11.7.1"),sQuery(id+"F0.wireOp",EDGE,"E11.7.2"),sQuery(id+"F0.wireOp",EDGE,"E11.7.3"),sQuery(id+"F0.wireOp",EDGE,"E11.7.4"),sQuery(id+"F0.wireOp",EDGE,"E11.7.5"),sQuery(id+"F0.wireOp",EDGE,"E11.8.0"),sQuery(id+"F0.wireOp",EDGE,"E11.8.1"),sQuery(id+"F0.wireOp",EDGE,"E11.8.2"),sQuery(id+"F0.wireOp",EDGE,"E11.8.3"),sQuery(id+"F0.wireOp",EDGE,"E11.8.4"),sQuery(id+"F0.wireOp",EDGE,"E11.8.5"),sQuery(id+"F0.wireOp",EDGE,"E11.9.0"),sQuery(id+"F0.wireOp",EDGE,"E11.9.1"),sQuery(id+"F0.wireOp",EDGE,"E11.9.2"),sQuery(id+"F0.wireOp",EDGE,"E11.9.3"),sQuery(id+"F0.wireOp",EDGE,"E11.9.4"),sQuery(id+"F0.wireOp",EDGE,"E11.9.5"),sQuery(id+"F0.wireOp",EDGE,"E11.10.0"),sQuery(id+"F0.wireOp",EDGE,"E11.10.1"),sQuery(id+"F0.wireOp",EDGE,"E11.10.2"),sQuery(id+"F0.wireOp",EDGE,"E11.10.3"),sQuery(id+"F0.wireOp",EDGE,"E11.10.4"),sQuery(id+"F0.wireOp",EDGE,"E11.10.5"),sQuery(id+"F0.wireOp",EDGE,"E11.11.0"),sQuery(id+"F0.wireOp",EDGE,"E11.11.1"),sQuery(id+"F0.wireOp",EDGE,"E11.11.2"),sQuery(id+"F0.wireOp",EDGE,"E11.11.3"),sQuery(id+"F0.wireOp",EDGE,"E11.11.4"),sQuery(id+"F0.wireOp",EDGE,"E11.11.5"),sQuery(id+"F0.wireOp",EDGE,"E11.12.0"),sQuery(id+"F0.wireOp",EDGE,"E11.12.1"),sQuery(id+"F0.wireOp",EDGE,"E11.12.2"),sQuery(id+"F0.wireOp",EDGE,"E11.12.3"),sQuery(id+"F0.wireOp",EDGE,"E11.12.4"),sQuery(id+"F0.wireOp",EDGE,"E11.12.5"),sQuery(id+"F0.wireOp",EDGE,"E11.13.0"),sQuery(id+"F0.wireOp",EDGE,"E11.13.1"),sQuery(id+"F0.wireOp",EDGE,"E11.13.2"),sQuery(id+"F0.wireOp",EDGE,"E11.13.3"),sQuery(id+"F0.wireOp",EDGE,"E11.13.4"),sQuery(id+"F0.wireOp",EDGE,"E11.13.5"),sQuery(id+"F0.wireOp",EDGE,"E11.14.0"),sQuery(id+"F0.wireOp",EDGE,"E11.14.1"),sQuery(id+"F0.wireOp",EDGE,"E11.14.2"),sQuery(id+"F0.wireOp",EDGE,"E11.14.3"),sQuery(id+"F0.wireOp",EDGE,"E11.14.4"),sQuery(id+"F0.wireOp",EDGE,"E11.14.5"),sQuery(id+"F0.wireOp",EDGE,"E11.15.0"),sQuery(id+"F0.wireOp",EDGE,"E11.15.1"),sQuery(id+"F0.wireOp",EDGE,"E11.15.2"),sQuery(id+"F0.wireOp",EDGE,"E11.15.3"),sQuery(id+"F0.wireOp",EDGE,"E11.15.4"),sQuery(id+"F0.wireOp",EDGE,"E11.15.5"),sQuery(id+"F0.wireOp",EDGE,"E11.16.0"),sQuery(id+"F0.wireOp",EDGE,"E11.16.1"),sQuery(id+"F0.wireOp",EDGE,"E11.16.2"),sQuery(id+"F0.wireOp",EDGE,"E11.16.3"),sQuery(id+"F0.wireOp",EDGE,"E11.16.4"),sQuery(id+"F0.wireOp",EDGE,"E11.16.5"),sQuery(id+"F0.wireOp",EDGE,"E11.17.0"),sQuery(id+"F0.wireOp",EDGE,"E11.17.1"),sQuery(id+"F0.wireOp",EDGE,"E11.17.2"),sQuery(id+"F0.wireOp",EDGE,"E11.17.3"),sQuery(id+"F0.wireOp",EDGE,"E11.17.4"),sQuery(id+"F0.wireOp",EDGE,"E11.17.5"),sQuery(id+"F0.wireOp",EDGE,"E11.18.0"),sQuery(id+"F0.wireOp",EDGE,"E11.18.1"),sQuery(id+"F0.wireOp",EDGE,"E11.18.2"),sQuery(id+"F0.wireOp",EDGE,"E11.18.3"),sQuery(id+"F0.wireOp",EDGE,"E11.18.4"),sQuery(id+"F0.wireOp",EDGE,"E11.18.5"),sQuery(id+"F0.wireOp",EDGE,"E11.19.0"),sQuery(id+"F0.wireOp",EDGE,"E11.19.1"),sQuery(id+"F0.wireOp",EDGE,"E11.19.2"),sQuery(id+"F0.wireOp",EDGE,"E11.19.3"),sQuery(id+"F0.wireOp",EDGE,"E11.19.4"),sQuery(id+"F0.wireOp",EDGE,"E11.19.5"),sQuery(id+"F0.wireOp",EDGE,"E11.20.0"),sQuery(id+"F0.wireOp",EDGE,"E11.20.1"),sQuery(id+"F0.wireOp",EDGE,"E11.20.2"),sQuery(id+"F0.wireOp",EDGE,"E11.20.3"),sQuery(id+"F0.wireOp",EDGE,"E11.20.4"),sQuery(id+"F0.wireOp",EDGE,"E11.20.5"),sQuery(id+"F0.wireOp",EDGE,"E11.21.0"),sQuery(id+"F0.wireOp",EDGE,"E11.21.1"),sQuery(id+"F0.wireOp",EDGE,"E11.21.2"),sQuery(id+"F0.wireOp",EDGE,"E11.21.3"),sQuery(id+"F0.wireOp",EDGE,"E11.21.4"),sQuery(id+"F0.wireOp",EDGE,"E11.21.5"),sQuery(id+"F0.wireOp",EDGE,"E11.22.0"),sQuery(id+"F0.wireOp",EDGE,"E11.22.1"),sQuery(id+"F0.wireOp",EDGE,"E11.22.2"),sQuery(id+"F0.wireOp",EDGE,"E11.22.3"),sQuery(id+"F0.wireOp",EDGE,"E11.22.4"),sQuery(id+"F0.wireOp",EDGE,"E11.22.5"),sQuery(id+"F0.wireOp",EDGE,"E11.23.0"),sQuery(id+"F0.wireOp",EDGE,"E11.23.1"),sQuery(id+"F0.wireOp",EDGE,"E11.23.2"),sQuery(id+"F0.wireOp",EDGE,"E11.23.3"),sQuery(id+"F0.wireOp",EDGE,"E11.23.4"),sQuery(id+"F0.wireOp",EDGE,"E11.23.5"),sQuery(id+"F0.wireOp",EDGE,"E11.24.0"),sQuery(id+"F0.wireOp",EDGE,"E11.24.1"),sQuery(id+"F0.wireOp",EDGE,"E11.24.2"),sQuery(id+"F0.wireOp",EDGE,"E11.24.3"),sQuery(id+"F0.wireOp",EDGE,"E11.24.4"),sQuery(id+"F0.wireOp",EDGE,"E11.24.5"),sQuery(id+"F0.wireOp",EDGE,"E11.25.0"),sQuery(id+"F0.wireOp",EDGE,"E11.25.1"),sQuery(id+"F0.wireOp",EDGE,"E11.25.2"),sQuery(id+"F0.wireOp",EDGE,"E11.25.3"),sQuery(id+"F0.wireOp",EDGE,"E11.25.4"),sQuery(id+"F0.wireOp",EDGE,"E11.25.5"),sQuery(id+"F0.wireOp",EDGE,"E11.26.0"),sQuery(id+"F0.wireOp",EDGE,"E11.26.1"),sQuery(id+"F0.wireOp",EDGE,"E11.26.2"),sQuery(id+"F0.wireOp",EDGE,"E11.26.3"),sQuery(id+"F0.wireOp",EDGE,"E11.26.4"),sQuery(id+"F0.wireOp",EDGE,"E11.26.5"),sQuery(id+"F0.wireOp",EDGE,"E11.27.0"),sQuery(id+"F0.wireOp",EDGE,"E11.27.1"),sQuery(id+"F0.wireOp",EDGE,"E11.27.2"),sQuery(id+"F0.wireOp",EDGE,"E11.27.3"),sQuery(id+"F0.wireOp",EDGE,"E11.27.4"),sQuery(id+"F0.wireOp",EDGE,"E11.27.5"),sQuery(id+"F0.wireOp",EDGE,"E11.28.0"),sQuery(id+"F0.wireOp",EDGE,"E11.28.1"),sQuery(id+"F0.wireOp",EDGE,"E11.28.2"),sQuery(id+"F0.wireOp",EDGE,"E11.28.3"),sQuery(id+"F0.wireOp",EDGE,"E11.28.4"),sQuery(id+"F0.wireOp",EDGE,"E11.28.5"),sQuery(id+"F0.wireOp",EDGE,"E11.29.0"),sQuery(id+"F0.wireOp",EDGE,"E11.29.1"),sQuery(id+"F0.wireOp",EDGE,"E11.29.2"),sQuery(id+"F0.wireOp",EDGE,"E11.29.3"),sQuery(id+"F0.wireOp",EDGE,"E11.29.4"),sQuery(id+"F0.wireOp",EDGE,"E11.29.5"),sQuery(id+"F0.wireOp",EDGE,"E11.30.0"),sQuery(id+"F0.wireOp",EDGE,"E11.30.1"),sQuery(id+"F0.wireOp",EDGE,"E11.30.2"),sQuery(id+"F0.wireOp",EDGE,"E11.30.3"),sQuery(id+"F0.wireOp",EDGE,"E11.30.4"),sQuery(id+"F0.wireOp",EDGE,"E11.30.5"),sQuery(id+"F0.wireOp",EDGE,"E11.31.0"),sQuery(id+"F0.wireOp",EDGE,"E11.31.1"),sQuery(id+"F0.wireOp",EDGE,"E11.31.2"),sQuery(id+"F0.wireOp",EDGE,"E11.31.3"),sQuery(id+"F0.wireOp",EDGE,"E11.31.4"),sQuery(id+"F0.wireOp",EDGE,"E11.31.5"),sQuery(id+"F0.wireOp",EDGE,"E11.32.0"),sQuery(id+"F0.wireOp",EDGE,"E11.32.1"),sQuery(id+"F0.wireOp",EDGE,"E11.32.2"),sQuery(id+"F0.wireOp",EDGE,"E11.32.3"),sQuery(id+"F0.wireOp",EDGE,"E11.32.4"),sQuery(id+"F0.wireOp",EDGE,"E11.32.5"),sQuery(id+"F0.wireOp",EDGE,"E11.33.0"),sQuery(id+"F0.wireOp",EDGE,"E11.33.1"),sQuery(id+"F0.wireOp",EDGE,"E11.33.2"),sQuery(id+"F0.wireOp",EDGE,"E11.33.3"),sQuery(id+"F0.wireOp",EDGE,"E11.33.4"),sQuery(id+"F0.wireOp",EDGE,"E11.33.5"),sQuery(id+"F0.wireOp",EDGE,"E11.34.0"),sQuery(id+"F0.wireOp",EDGE,"E11.34.1"),sQuery(id+"F0.wireOp",EDGE,"E11.34.2"),sQuery(id+"F0.wireOp",EDGE,"E11.34.3"),sQuery(id+"F0.wireOp",EDGE,"E11.34.4"),sQuery(id+"F0.wireOp",EDGE,"E11.34.5"),sQuery(id+"F0.wireOp",EDGE,"E11.35.0"),sQuery(id+"F0.wireOp",EDGE,"E11.35.1"),sQuery(id+"F0.wireOp",EDGE,"E11.35.2"),sQuery(id+"F0.wireOp",EDGE,"E11.35.3"),sQuery(id+"F0.wireOp",EDGE,"E11.35.4"),sQuery(id+"F0.wireOp",EDGE,"E11.35.5"),sQuery(id+"F0.wireOp",EDGE,"E12")])],"isStart":false});
            var Q1;
            Q1=makeQuery(id+"F1.opExtrude","CAP_FACE",FACE,{"disambiguationData":[OSD([sQuery(id+"F0.wireOp",EDGE,"E5"),sQuery(id+"F0.wireOp",EDGE,"E6"),sQuery(id+"F0.wireOp",EDGE,"E7.MirrorCS"),sQuery(id+"F0.wireOp",EDGE,"E8.MirrorCS"),sQuery(id+"F0.wireOp",EDGE,"E9.filletArc"),sQuery(id+"F0.wireOp",EDGE,"E10.MirrorCS"),sQuery(id+"F0.wireOp",EDGE,"E11.1.0"),sQuery(id+"F0.wireOp",EDGE,"E11.1.1"),sQuery(id+"F0.wireOp",EDGE,"E11.1.2"),sQuery(id+"F0.wireOp",EDGE,"E11.1.3"),sQuery(id+"F0.wireOp",EDGE,"E11.1.4"),sQuery(id+"F0.wireOp",EDGE,"E11.1.5"),sQuery(id+"F0.wireOp",EDGE,"E11.2.0"),sQuery(id+"F0.wireOp",EDGE,"E11.2.1"),sQuery(id+"F0.wireOp",EDGE,"E11.2.2"),sQuery(id+"F0.wireOp",EDGE,"E11.2.3"),sQuery(id+"F0.wireOp",EDGE,"E11.2.4"),sQuery(id+"F0.wireOp",EDGE,"E11.2.5"),sQuery(id+"F0.wireOp",EDGE,"E11.3.0"),sQuery(id+"F0.wireOp",EDGE,"E11.3.1"),sQuery(id+"F0.wireOp",EDGE,"E11.3.2"),sQuery(id+"F0.wireOp",EDGE,"E11.3.3"),sQuery(id+"F0.wireOp",EDGE,"E11.3.4"),sQuery(id+"F0.wireOp",EDGE,"E11.3.5"),sQuery(id+"F0.wireOp",EDGE,"E11.4.0"),sQuery(id+"F0.wireOp",EDGE,"E11.4.1"),sQuery(id+"F0.wireOp",EDGE,"E11.4.2"),sQuery(id+"F0.wireOp",EDGE,"E11.4.3"),sQuery(id+"F0.wireOp",EDGE,"E11.4.4"),sQuery(id+"F0.wireOp",EDGE,"E11.4.5"),sQuery(id+"F0.wireOp",EDGE,"E11.5.0"),sQuery(id+"F0.wireOp",EDGE,"E11.5.1"),sQuery(id+"F0.wireOp",EDGE,"E11.5.2"),sQuery(id+"F0.wireOp",EDGE,"E11.5.3"),sQuery(id+"F0.wireOp",EDGE,"E11.5.4"),sQuery(id+"F0.wireOp",EDGE,"E11.5.5"),sQuery(id+"F0.wireOp",EDGE,"E11.6.0"),sQuery(id+"F0.wireOp",EDGE,"E11.6.1"),sQuery(id+"F0.wireOp",EDGE,"E11.6.2"),sQuery(id+"F0.wireOp",EDGE,"E11.6.3"),sQuery(id+"F0.wireOp",EDGE,"E11.6.4"),sQuery(id+"F0.wireOp",EDGE,"E11.6.5"),sQuery(id+"F0.wireOp",EDGE,"E11.7.0"),sQuery(id+"F0.wireOp",EDGE,"E11.7.1"),sQuery(id+"F0.wireOp",EDGE,"E11.7.2"),sQuery(id+"F0.wireOp",EDGE,"E11.7.3"),sQuery(id+"F0.wireOp",EDGE,"E11.7.4"),sQuery(id+"F0.wireOp",EDGE,"E11.7.5"),sQuery(id+"F0.wireOp",EDGE,"E11.8.0"),sQuery(id+"F0.wireOp",EDGE,"E11.8.1"),sQuery(id+"F0.wireOp",EDGE,"E11.8.2"),sQuery(id+"F0.wireOp",EDGE,"E11.8.3"),sQuery(id+"F0.wireOp",EDGE,"E11.8.4"),sQuery(id+"F0.wireOp",EDGE,"E11.8.5"),sQuery(id+"F0.wireOp",EDGE,"E11.9.0"),sQuery(id+"F0.wireOp",EDGE,"E11.9.1"),sQuery(id+"F0.wireOp",EDGE,"E11.9.2"),sQuery(id+"F0.wireOp",EDGE,"E11.9.3"),sQuery(id+"F0.wireOp",EDGE,"E11.9.4"),sQuery(id+"F0.wireOp",EDGE,"E11.9.5"),sQuery(id+"F0.wireOp",EDGE,"E11.10.0"),sQuery(id+"F0.wireOp",EDGE,"E11.10.1"),sQuery(id+"F0.wireOp",EDGE,"E11.10.2"),sQuery(id+"F0.wireOp",EDGE,"E11.10.3"),sQuery(id+"F0.wireOp",EDGE,"E11.10.4"),sQuery(id+"F0.wireOp",EDGE,"E11.10.5"),sQuery(id+"F0.wireOp",EDGE,"E11.11.0"),sQuery(id+"F0.wireOp",EDGE,"E11.11.1"),sQuery(id+"F0.wireOp",EDGE,"E11.11.2"),sQuery(id+"F0.wireOp",EDGE,"E11.11.3"),sQuery(id+"F0.wireOp",EDGE,"E11.11.4"),sQuery(id+"F0.wireOp",EDGE,"E11.11.5"),sQuery(id+"F0.wireOp",EDGE,"E11.12.0"),sQuery(id+"F0.wireOp",EDGE,"E11.12.1"),sQuery(id+"F0.wireOp",EDGE,"E11.12.2"),sQuery(id+"F0.wireOp",EDGE,"E11.12.3"),sQuery(id+"F0.wireOp",EDGE,"E11.12.4"),sQuery(id+"F0.wireOp",EDGE,"E11.12.5"),sQuery(id+"F0.wireOp",EDGE,"E11.13.0"),sQuery(id+"F0.wireOp",EDGE,"E11.13.1"),sQuery(id+"F0.wireOp",EDGE,"E11.13.2"),sQuery(id+"F0.wireOp",EDGE,"E11.13.3"),sQuery(id+"F0.wireOp",EDGE,"E11.13.4"),sQuery(id+"F0.wireOp",EDGE,"E11.13.5"),sQuery(id+"F0.wireOp",EDGE,"E11.14.0"),sQuery(id+"F0.wireOp",EDGE,"E11.14.1"),sQuery(id+"F0.wireOp",EDGE,"E11.14.2"),sQuery(id+"F0.wireOp",EDGE,"E11.14.3"),sQuery(id+"F0.wireOp",EDGE,"E11.14.4"),sQuery(id+"F0.wireOp",EDGE,"E11.14.5"),sQuery(id+"F0.wireOp",EDGE,"E11.15.0"),sQuery(id+"F0.wireOp",EDGE,"E11.15.1"),sQuery(id+"F0.wireOp",EDGE,"E11.15.2"),sQuery(id+"F0.wireOp",EDGE,"E11.15.3"),sQuery(id+"F0.wireOp",EDGE,"E11.15.4"),sQuery(id+"F0.wireOp",EDGE,"E11.15.5"),sQuery(id+"F0.wireOp",EDGE,"E11.16.0"),sQuery(id+"F0.wireOp",EDGE,"E11.16.1"),sQuery(id+"F0.wireOp",EDGE,"E11.16.2"),sQuery(id+"F0.wireOp",EDGE,"E11.16.3"),sQuery(id+"F0.wireOp",EDGE,"E11.16.4"),sQuery(id+"F0.wireOp",EDGE,"E11.16.5"),sQuery(id+"F0.wireOp",EDGE,"E11.17.0"),sQuery(id+"F0.wireOp",EDGE,"E11.17.1"),sQuery(id+"F0.wireOp",EDGE,"E11.17.2"),sQuery(id+"F0.wireOp",EDGE,"E11.17.3"),sQuery(id+"F0.wireOp",EDGE,"E11.17.4"),sQuery(id+"F0.wireOp",EDGE,"E11.17.5"),sQuery(id+"F0.wireOp",EDGE,"E11.18.0"),sQuery(id+"F0.wireOp",EDGE,"E11.18.1"),sQuery(id+"F0.wireOp",EDGE,"E11.18.2"),sQuery(id+"F0.wireOp",EDGE,"E11.18.3"),sQuery(id+"F0.wireOp",EDGE,"E11.18.4"),sQuery(id+"F0.wireOp",EDGE,"E11.18.5"),sQuery(id+"F0.wireOp",EDGE,"E11.19.0"),sQuery(id+"F0.wireOp",EDGE,"E11.19.1"),sQuery(id+"F0.wireOp",EDGE,"E11.19.2"),sQuery(id+"F0.wireOp",EDGE,"E11.19.3"),sQuery(id+"F0.wireOp",EDGE,"E11.19.4"),sQuery(id+"F0.wireOp",EDGE,"E11.19.5"),sQuery(id+"F0.wireOp",EDGE,"E11.20.0"),sQuery(id+"F0.wireOp",EDGE,"E11.20.1"),sQuery(id+"F0.wireOp",EDGE,"E11.20.2"),sQuery(id+"F0.wireOp",EDGE,"E11.20.3"),sQuery(id+"F0.wireOp",EDGE,"E11.20.4"),sQuery(id+"F0.wireOp",EDGE,"E11.20.5"),sQuery(id+"F0.wireOp",EDGE,"E11.21.0"),sQuery(id+"F0.wireOp",EDGE,"E11.21.1"),sQuery(id+"F0.wireOp",EDGE,"E11.21.2"),sQuery(id+"F0.wireOp",EDGE,"E11.21.3"),sQuery(id+"F0.wireOp",EDGE,"E11.21.4"),sQuery(id+"F0.wireOp",EDGE,"E11.21.5"),sQuery(id+"F0.wireOp",EDGE,"E11.22.0"),sQuery(id+"F0.wireOp",EDGE,"E11.22.1"),sQuery(id+"F0.wireOp",EDGE,"E11.22.2"),sQuery(id+"F0.wireOp",EDGE,"E11.22.3"),sQuery(id+"F0.wireOp",EDGE,"E11.22.4"),sQuery(id+"F0.wireOp",EDGE,"E11.22.5"),sQuery(id+"F0.wireOp",EDGE,"E11.23.0"),sQuery(id+"F0.wireOp",EDGE,"E11.23.1"),sQuery(id+"F0.wireOp",EDGE,"E11.23.2"),sQuery(id+"F0.wireOp",EDGE,"E11.23.3"),sQuery(id+"F0.wireOp",EDGE,"E11.23.4"),sQuery(id+"F0.wireOp",EDGE,"E11.23.5"),sQuery(id+"F0.wireOp",EDGE,"E11.24.0"),sQuery(id+"F0.wireOp",EDGE,"E11.24.1"),sQuery(id+"F0.wireOp",EDGE,"E11.24.2"),sQuery(id+"F0.wireOp",EDGE,"E11.24.3"),sQuery(id+"F0.wireOp",EDGE,"E11.24.4"),sQuery(id+"F0.wireOp",EDGE,"E11.24.5"),sQuery(id+"F0.wireOp",EDGE,"E11.25.0"),sQuery(id+"F0.wireOp",EDGE,"E11.25.1"),sQuery(id+"F0.wireOp",EDGE,"E11.25.2"),sQuery(id+"F0.wireOp",EDGE,"E11.25.3"),sQuery(id+"F0.wireOp",EDGE,"E11.25.4"),sQuery(id+"F0.wireOp",EDGE,"E11.25.5"),sQuery(id+"F0.wireOp",EDGE,"E11.26.0"),sQuery(id+"F0.wireOp",EDGE,"E11.26.1"),sQuery(id+"F0.wireOp",EDGE,"E11.26.2"),sQuery(id+"F0.wireOp",EDGE,"E11.26.3"),sQuery(id+"F0.wireOp",EDGE,"E11.26.4"),sQuery(id+"F0.wireOp",EDGE,"E11.26.5"),sQuery(id+"F0.wireOp",EDGE,"E11.27.0"),sQuery(id+"F0.wireOp",EDGE,"E11.27.1"),sQuery(id+"F0.wireOp",EDGE,"E11.27.2"),sQuery(id+"F0.wireOp",EDGE,"E11.27.3"),sQuery(id+"F0.wireOp",EDGE,"E11.27.4"),sQuery(id+"F0.wireOp",EDGE,"E11.27.5"),sQuery(id+"F0.wireOp",EDGE,"E11.28.0"),sQuery(id+"F0.wireOp",EDGE,"E11.28.1"),sQuery(id+"F0.wireOp",EDGE,"E11.28.2"),sQuery(id+"F0.wireOp",EDGE,"E11.28.3"),sQuery(id+"F0.wireOp",EDGE,"E11.28.4"),sQuery(id+"F0.wireOp",EDGE,"E11.28.5"),sQuery(id+"F0.wireOp",EDGE,"E11.29.0"),sQuery(id+"F0.wireOp",EDGE,"E11.29.1"),sQuery(id+"F0.wireOp",EDGE,"E11.29.2"),sQuery(id+"F0.wireOp",EDGE,"E11.29.3"),sQuery(id+"F0.wireOp",EDGE,"E11.29.4"),sQuery(id+"F0.wireOp",EDGE,"E11.29.5"),sQuery(id+"F0.wireOp",EDGE,"E11.30.0"),sQuery(id+"F0.wireOp",EDGE,"E11.30.1"),sQuery(id+"F0.wireOp",EDGE,"E11.30.2"),sQuery(id+"F0.wireOp",EDGE,"E11.30.3"),sQuery(id+"F0.wireOp",EDGE,"E11.30.4"),sQuery(id+"F0.wireOp",EDGE,"E11.30.5"),sQuery(id+"F0.wireOp",EDGE,"E11.31.0"),sQuery(id+"F0.wireOp",EDGE,"E11.31.1"),sQuery(id+"F0.wireOp",EDGE,"E11.31.2"),sQuery(id+"F0.wireOp",EDGE,"E11.31.3"),sQuery(id+"F0.wireOp",EDGE,"E11.31.4"),sQuery(id+"F0.wireOp",EDGE,"E11.31.5"),sQuery(id+"F0.wireOp",EDGE,"E11.32.0"),sQuery(id+"F0.wireOp",EDGE,"E11.32.1"),sQuery(id+"F0.wireOp",EDGE,"E11.32.2"),sQuery(id+"F0.wireOp",EDGE,"E11.32.3"),sQuery(id+"F0.wireOp",EDGE,"E11.32.4"),sQuery(id+"F0.wireOp",EDGE,"E11.32.5"),sQuery(id+"F0.wireOp",EDGE,"E11.33.0"),sQuery(id+"F0.wireOp",EDGE,"E11.33.1"),sQuery(id+"F0.wireOp",EDGE,"E11.33.2"),sQuery(id+"F0.wireOp",EDGE,"E11.33.3"),sQuery(id+"F0.wireOp",EDGE,"E11.33.4"),sQuery(id+"F0.wireOp",EDGE,"E11.33.5"),sQuery(id+"F0.wireOp",EDGE,"E11.34.0"),sQuery(id+"F0.wireOp",EDGE,"E11.34.1"),sQuery(id+"F0.wireOp",EDGE,"E11.34.2"),sQuery(id+"F0.wireOp",EDGE,"E11.34.3"),sQuery(id+"F0.wireOp",EDGE,"E11.34.4"),sQuery(id+"F0.wireOp",EDGE,"E11.34.5"),sQuery(id+"F0.wireOp",EDGE,"E11.35.0"),sQuery(id+"F0.wireOp",EDGE,"E11.35.1"),sQuery(id+"F0.wireOp",EDGE,"E11.35.2"),sQuery(id+"F0.wireOp",EDGE,"E11.35.3"),sQuery(id+"F0.wireOp",EDGE,"E11.35.4"),sQuery(id+"F0.wireOp",EDGE,"E11.35.5"),sQuery(id+"F0.wireOp",EDGE,"E12")])],"isStart":true});
            chamfer(context, id + "F2", {"entities" : qUnion([Q0, Q1]), "width" : .5 * mm, "tangentPropagation" : true});
        }
        {
            var Q0;
            Q0=makeQuery(id+"F1.opExtrude","CAP_FACE",FACE,{"disambiguationData":[OSD([sQuery(id+"F0.wireOp",EDGE,"E5"),sQuery(id+"F0.wireOp",EDGE,"E6"),sQuery(id+"F0.wireOp",EDGE,"E7.MirrorCS"),sQuery(id+"F0.wireOp",EDGE,"E8.MirrorCS"),sQuery(id+"F0.wireOp",EDGE,"E9.filletArc"),sQuery(id+"F0.wireOp",EDGE,"E10.MirrorCS"),sQuery(id+"F0.wireOp",EDGE,"E11.1.0"),sQuery(id+"F0.wireOp",EDGE,"E11.1.1"),sQuery(id+"F0.wireOp",EDGE,"E11.1.2"),sQuery(id+"F0.wireOp",EDGE,"E11.1.3"),sQuery(id+"F0.wireOp",EDGE,"E11.1.4"),sQuery(id+"F0.wireOp",EDGE,"E11.1.5"),sQuery(id+"F0.wireOp",EDGE,"E11.2.0"),sQuery(id+"F0.wireOp",EDGE,"E11.2.1"),sQuery(id+"F0.wireOp",EDGE,"E11.2.2"),sQuery(id+"F0.wireOp",EDGE,"E11.2.3"),sQuery(id+"F0.wireOp",EDGE,"E11.2.4"),sQuery(id+"F0.wireOp",EDGE,"E11.2.5"),sQuery(id+"F0.wireOp",EDGE,"E11.3.0"),sQuery(id+"F0.wireOp",EDGE,"E11.3.1"),sQuery(id+"F0.wireOp",EDGE,"E11.3.2"),sQuery(id+"F0.wireOp",EDGE,"E11.3.3"),sQuery(id+"F0.wireOp",EDGE,"E11.3.4"),sQuery(id+"F0.wireOp",EDGE,"E11.3.5"),sQuery(id+"F0.wireOp",EDGE,"E11.4.0"),sQuery(id+"F0.wireOp",EDGE,"E11.4.1"),sQuery(id+"F0.wireOp",EDGE,"E11.4.2"),sQuery(id+"F0.wireOp",EDGE,"E11.4.3"),sQuery(id+"F0.wireOp",EDGE,"E11.4.4"),sQuery(id+"F0.wireOp",EDGE,"E11.4.5"),sQuery(id+"F0.wireOp",EDGE,"E11.5.0"),sQuery(id+"F0.wireOp",EDGE,"E11.5.1"),sQuery(id+"F0.wireOp",EDGE,"E11.5.2"),sQuery(id+"F0.wireOp",EDGE,"E11.5.3"),sQuery(id+"F0.wireOp",EDGE,"E11.5.4"),sQuery(id+"F0.wireOp",EDGE,"E11.5.5"),sQuery(id+"F0.wireOp",EDGE,"E11.6.0"),sQuery(id+"F0.wireOp",EDGE,"E11.6.1"),sQuery(id+"F0.wireOp",EDGE,"E11.6.2"),sQuery(id+"F0.wireOp",EDGE,"E11.6.3"),sQuery(id+"F0.wireOp",EDGE,"E11.6.4"),sQuery(id+"F0.wireOp",EDGE,"E11.6.5"),sQuery(id+"F0.wireOp",EDGE,"E11.7.0"),sQuery(id+"F0.wireOp",EDGE,"E11.7.1"),sQuery(id+"F0.wireOp",EDGE,"E11.7.2"),sQuery(id+"F0.wireOp",EDGE,"E11.7.3"),sQuery(id+"F0.wireOp",EDGE,"E11.7.4"),sQuery(id+"F0.wireOp",EDGE,"E11.7.5"),sQuery(id+"F0.wireOp",EDGE,"E11.8.0"),sQuery(id+"F0.wireOp",EDGE,"E11.8.1"),sQuery(id+"F0.wireOp",EDGE,"E11.8.2"),sQuery(id+"F0.wireOp",EDGE,"E11.8.3"),sQuery(id+"F0.wireOp",EDGE,"E11.8.4"),sQuery(id+"F0.wireOp",EDGE,"E11.8.5"),sQuery(id+"F0.wireOp",EDGE,"E11.9.0"),sQuery(id+"F0.wireOp",EDGE,"E11.9.1"),sQuery(id+"F0.wireOp",EDGE,"E11.9.2"),sQuery(id+"F0.wireOp",EDGE,"E11.9.3"),sQuery(id+"F0.wireOp",EDGE,"E11.9.4"),sQuery(id+"F0.wireOp",EDGE,"E11.9.5"),sQuery(id+"F0.wireOp",EDGE,"E11.10.0"),sQuery(id+"F0.wireOp",EDGE,"E11.10.1"),sQuery(id+"F0.wireOp",EDGE,"E11.10.2"),sQuery(id+"F0.wireOp",EDGE,"E11.10.3"),sQuery(id+"F0.wireOp",EDGE,"E11.10.4"),sQuery(id+"F0.wireOp",EDGE,"E11.10.5"),sQuery(id+"F0.wireOp",EDGE,"E11.11.0"),sQuery(id+"F0.wireOp",EDGE,"E11.11.1"),sQuery(id+"F0.wireOp",EDGE,"E11.11.2"),sQuery(id+"F0.wireOp",EDGE,"E11.11.3"),sQuery(id+"F0.wireOp",EDGE,"E11.11.4"),sQuery(id+"F0.wireOp",EDGE,"E11.11.5"),sQuery(id+"F0.wireOp",EDGE,"E11.12.0"),sQuery(id+"F0.wireOp",EDGE,"E11.12.1"),sQuery(id+"F0.wireOp",EDGE,"E11.12.2"),sQuery(id+"F0.wireOp",EDGE,"E11.12.3"),sQuery(id+"F0.wireOp",EDGE,"E11.12.4"),sQuery(id+"F0.wireOp",EDGE,"E11.12.5"),sQuery(id+"F0.wireOp",EDGE,"E11.13.0"),sQuery(id+"F0.wireOp",EDGE,"E11.13.1"),sQuery(id+"F0.wireOp",EDGE,"E11.13.2"),sQuery(id+"F0.wireOp",EDGE,"E11.13.3"),sQuery(id+"F0.wireOp",EDGE,"E11.13.4"),sQuery(id+"F0.wireOp",EDGE,"E11.13.5"),sQuery(id+"F0.wireOp",EDGE,"E11.14.0"),sQuery(id+"F0.wireOp",EDGE,"E11.14.1"),sQuery(id+"F0.wireOp",EDGE,"E11.14.2"),sQuery(id+"F0.wireOp",EDGE,"E11.14.3"),sQuery(id+"F0.wireOp",EDGE,"E11.14.4"),sQuery(id+"F0.wireOp",EDGE,"E11.14.5"),sQuery(id+"F0.wireOp",EDGE,"E11.15.0"),sQuery(id+"F0.wireOp",EDGE,"E11.15.1"),sQuery(id+"F0.wireOp",EDGE,"E11.15.2"),sQuery(id+"F0.wireOp",EDGE,"E11.15.3"),sQuery(id+"F0.wireOp",EDGE,"E11.15.4"),sQuery(id+"F0.wireOp",EDGE,"E11.15.5"),sQuery(id+"F0.wireOp",EDGE,"E11.16.0"),sQuery(id+"F0.wireOp",EDGE,"E11.16.1"),sQuery(id+"F0.wireOp",EDGE,"E11.16.2"),sQuery(id+"F0.wireOp",EDGE,"E11.16.3"),sQuery(id+"F0.wireOp",EDGE,"E11.16.4"),sQuery(id+"F0.wireOp",EDGE,"E11.16.5"),sQuery(id+"F0.wireOp",EDGE,"E11.17.0"),sQuery(id+"F0.wireOp",EDGE,"E11.17.1"),sQuery(id+"F0.wireOp",EDGE,"E11.17.2"),sQuery(id+"F0.wireOp",EDGE,"E11.17.3"),sQuery(id+"F0.wireOp",EDGE,"E11.17.4"),sQuery(id+"F0.wireOp",EDGE,"E11.17.5"),sQuery(id+"F0.wireOp",EDGE,"E11.18.0"),sQuery(id+"F0.wireOp",EDGE,"E11.18.1"),sQuery(id+"F0.wireOp",EDGE,"E11.18.2"),sQuery(id+"F0.wireOp",EDGE,"E11.18.3"),sQuery(id+"F0.wireOp",EDGE,"E11.18.4"),sQuery(id+"F0.wireOp",EDGE,"E11.18.5"),sQuery(id+"F0.wireOp",EDGE,"E11.19.0"),sQuery(id+"F0.wireOp",EDGE,"E11.19.1"),sQuery(id+"F0.wireOp",EDGE,"E11.19.2"),sQuery(id+"F0.wireOp",EDGE,"E11.19.3"),sQuery(id+"F0.wireOp",EDGE,"E11.19.4"),sQuery(id+"F0.wireOp",EDGE,"E11.19.5"),sQuery(id+"F0.wireOp",EDGE,"E11.20.0"),sQuery(id+"F0.wireOp",EDGE,"E11.20.1"),sQuery(id+"F0.wireOp",EDGE,"E11.20.2"),sQuery(id+"F0.wireOp",EDGE,"E11.20.3"),sQuery(id+"F0.wireOp",EDGE,"E11.20.4"),sQuery(id+"F0.wireOp",EDGE,"E11.20.5"),sQuery(id+"F0.wireOp",EDGE,"E11.21.0"),sQuery(id+"F0.wireOp",EDGE,"E11.21.1"),sQuery(id+"F0.wireOp",EDGE,"E11.21.2"),sQuery(id+"F0.wireOp",EDGE,"E11.21.3"),sQuery(id+"F0.wireOp",EDGE,"E11.21.4"),sQuery(id+"F0.wireOp",EDGE,"E11.21.5"),sQuery(id+"F0.wireOp",EDGE,"E11.22.0"),sQuery(id+"F0.wireOp",EDGE,"E11.22.1"),sQuery(id+"F0.wireOp",EDGE,"E11.22.2"),sQuery(id+"F0.wireOp",EDGE,"E11.22.3"),sQuery(id+"F0.wireOp",EDGE,"E11.22.4"),sQuery(id+"F0.wireOp",EDGE,"E11.22.5"),sQuery(id+"F0.wireOp",EDGE,"E11.23.0"),sQuery(id+"F0.wireOp",EDGE,"E11.23.1"),sQuery(id+"F0.wireOp",EDGE,"E11.23.2"),sQuery(id+"F0.wireOp",EDGE,"E11.23.3"),sQuery(id+"F0.wireOp",EDGE,"E11.23.4"),sQuery(id+"F0.wireOp",EDGE,"E11.23.5"),sQuery(id+"F0.wireOp",EDGE,"E11.24.0"),sQuery(id+"F0.wireOp",EDGE,"E11.24.1"),sQuery(id+"F0.wireOp",EDGE,"E11.24.2"),sQuery(id+"F0.wireOp",EDGE,"E11.24.3"),sQuery(id+"F0.wireOp",EDGE,"E11.24.4"),sQuery(id+"F0.wireOp",EDGE,"E11.24.5"),sQuery(id+"F0.wireOp",EDGE,"E11.25.0"),sQuery(id+"F0.wireOp",EDGE,"E11.25.1"),sQuery(id+"F0.wireOp",EDGE,"E11.25.2"),sQuery(id+"F0.wireOp",EDGE,"E11.25.3"),sQuery(id+"F0.wireOp",EDGE,"E11.25.4"),sQuery(id+"F0.wireOp",EDGE,"E11.25.5"),sQuery(id+"F0.wireOp",EDGE,"E11.26.0"),sQuery(id+"F0.wireOp",EDGE,"E11.26.1"),sQuery(id+"F0.wireOp",EDGE,"E11.26.2"),sQuery(id+"F0.wireOp",EDGE,"E11.26.3"),sQuery(id+"F0.wireOp",EDGE,"E11.26.4"),sQuery(id+"F0.wireOp",EDGE,"E11.26.5"),sQuery(id+"F0.wireOp",EDGE,"E11.27.0"),sQuery(id+"F0.wireOp",EDGE,"E11.27.1"),sQuery(id+"F0.wireOp",EDGE,"E11.27.2"),sQuery(id+"F0.wireOp",EDGE,"E11.27.3"),sQuery(id+"F0.wireOp",EDGE,"E11.27.4"),sQuery(id+"F0.wireOp",EDGE,"E11.27.5"),sQuery(id+"F0.wireOp",EDGE,"E11.28.0"),sQuery(id+"F0.wireOp",EDGE,"E11.28.1"),sQuery(id+"F0.wireOp",EDGE,"E11.28.2"),sQuery(id+"F0.wireOp",EDGE,"E11.28.3"),sQuery(id+"F0.wireOp",EDGE,"E11.28.4"),sQuery(id+"F0.wireOp",EDGE,"E11.28.5"),sQuery(id+"F0.wireOp",EDGE,"E11.29.0"),sQuery(id+"F0.wireOp",EDGE,"E11.29.1"),sQuery(id+"F0.wireOp",EDGE,"E11.29.2"),sQuery(id+"F0.wireOp",EDGE,"E11.29.3"),sQuery(id+"F0.wireOp",EDGE,"E11.29.4"),sQuery(id+"F0.wireOp",EDGE,"E11.29.5"),sQuery(id+"F0.wireOp",EDGE,"E11.30.0"),sQuery(id+"F0.wireOp",EDGE,"E11.30.1"),sQuery(id+"F0.wireOp",EDGE,"E11.30.2"),sQuery(id+"F0.wireOp",EDGE,"E11.30.3"),sQuery(id+"F0.wireOp",EDGE,"E11.30.4"),sQuery(id+"F0.wireOp",EDGE,"E11.30.5"),sQuery(id+"F0.wireOp",EDGE,"E11.31.0"),sQuery(id+"F0.wireOp",EDGE,"E11.31.1"),sQuery(id+"F0.wireOp",EDGE,"E11.31.2"),sQuery(id+"F0.wireOp",EDGE,"E11.31.3"),sQuery(id+"F0.wireOp",EDGE,"E11.31.4"),sQuery(id+"F0.wireOp",EDGE,"E11.31.5"),sQuery(id+"F0.wireOp",EDGE,"E11.32.0"),sQuery(id+"F0.wireOp",EDGE,"E11.32.1"),sQuery(id+"F0.wireOp",EDGE,"E11.32.2"),sQuery(id+"F0.wireOp",EDGE,"E11.32.3"),sQuery(id+"F0.wireOp",EDGE,"E11.32.4"),sQuery(id+"F0.wireOp",EDGE,"E11.32.5"),sQuery(id+"F0.wireOp",EDGE,"E11.33.0"),sQuery(id+"F0.wireOp",EDGE,"E11.33.1"),sQuery(id+"F0.wireOp",EDGE,"E11.33.2"),sQuery(id+"F0.wireOp",EDGE,"E11.33.3"),sQuery(id+"F0.wireOp",EDGE,"E11.33.4"),sQuery(id+"F0.wireOp",EDGE,"E11.33.5"),sQuery(id+"F0.wireOp",EDGE,"E11.34.0"),sQuery(id+"F0.wireOp",EDGE,"E11.34.1"),sQuery(id+"F0.wireOp",EDGE,"E11.34.2"),sQuery(id+"F0.wireOp",EDGE,"E11.34.3"),sQuery(id+"F0.wireOp",EDGE,"E11.34.4"),sQuery(id+"F0.wireOp",EDGE,"E11.34.5"),sQuery(id+"F0.wireOp",EDGE,"E11.35.0"),sQuery(id+"F0.wireOp",EDGE,"E11.35.1"),sQuery(id+"F0.wireOp",EDGE,"E11.35.2"),sQuery(id+"F0.wireOp",EDGE,"E11.35.3"),sQuery(id+"F0.wireOp",EDGE,"E11.35.4"),sQuery(id+"F0.wireOp",EDGE,"E11.35.5"),sQuery(id+"F0.wireOp",EDGE,"E12")])],"isStart":false});
            var sketch = newSketch(context, id + "F3", { "sketchPlane" : qUnion([Q0])});
            skCircle(sketch, "E13", {"center": v(0, 0) * mm, "radius": 25.68 * mm});
            skCircle(sketch, "E14", {"center": v(0, 0) * mm, "radius": 6.72 * mm});
            skArc(sketch, "E15", {"start": v(0, 6.72) * mm, "mid": v(7.94, 13.6) * mm, "end": v(9.02, 24.05) * mm});
            skArc(sketch, "E16", {"start": v(23.29, 10.82) * mm, "mid": v(12.99, 10.94) * mm, "end": v(4.75, 4.76) * mm});
            skArc(sketch, "E17.1.0", {"start": v(-21.02, 14.76) * mm, "mid": v(-15.97, 5.78) * mm, "end": v(-6.5, 1.74) * mm});
            skArc(sketch, "E17.1.1", {"start": v(-5.82, -3.36) * mm, "mid": v(-15.75, 0.08) * mm, "end": v(-25.33, -4.21) * mm});
            skArc(sketch, "E17.2.0", {"start": v(-2.27, -25.58) * mm, "mid": v(2.98, -16.72) * mm, "end": v(1.75, -6.5) * mm});
            skArc(sketch, "E17.2.1", {"start": v(5.82, -3.36) * mm, "mid": v(7.8, -13.68) * mm, "end": v(16.32, -19.83) * mm});
            skSolve(sketch);
        }
        {
            var Q0;
            {var subQ0=sQuery(id+"F3.wireOp",EDGE,"E15");Q0=makeQuery(id+"F3.imprint","IMPRINT",FACE,{"disambiguationData":[TD([[makeQuery(id+"F3.imprint","IMPRINT",EDGE,{"derivedFrom":subQ0}),1.0]])]});}
            var Q1;
            {var subQ0=sQuery(id+"F3.wireOp",EDGE,"E16");Q1=makeQuery(id+"F3.imprint","IMPRINT",FACE,{"disambiguationData":[TD([[makeQuery(id+"F3.imprint","IMPRINT",EDGE,{"derivedFrom":subQ0}),1.0]])]});}
            var Q2;
            {var subQ0=sQuery(id+"F3.wireOp",EDGE,"E17.1.1");Q2=makeQuery(id+"F3.imprint","IMPRINT",FACE,{"disambiguationData":[TD([[makeQuery(id+"F3.imprint","IMPRINT",EDGE,{"derivedFrom":subQ0}),1.0]])]});}
            extrude(context, id + "F4", {"entities" : qUnion([Q0, Q1, Q2]), "operationType" : NewBodyOperationType.REMOVE, "endBound" : BoundingType.UP_TO_NEXT, "oppositeDirection" : true, "depth" : 25 * mm});
        }
        {
            var Q0;
            {var subQ0=sQuery(id+"F3.wireOp",EDGE,"E13");Q0=makeQuery(id+"F4.boolean.opBoolean","COPY",FACE,{"derivedFrom":makeQuery(id+"F4.opExtrude","SWEPT_FACE",FACE,{"disambiguationData":[OSD([subQ0]),TDD([makeQuery(id+"F3.imprint","IMPRINT",EDGE,{"disambiguationData":[TD([[makeQuery(id+"F3.imprint","INTERSECT",VERTEX,{"derivedFrom":[subQ0,sQuery(id+"F3.wireOp",EDGE,"E15")]}),-1.0]])],"derivedFrom":subQ0})])]})});}
            var Q1;
            Q1=makeQuery(id+"F4.boolean.opBoolean","COPY",FACE,{"derivedFrom":makeQuery(id+"F4.opExtrude","SWEPT_FACE",FACE,{"disambiguationData":[OSD([sQuery(id+"F3.wireOp",EDGE,"E17.1.1")])]})});
            chamfer(context, id + "F5", {"entities" : qUnion([Q0, Q1]), "width" : 1 * mm, "tangentPropagation" : true});
        }
        {
            var Q0;
            Q0=makeQuery(id+"F4.boolean.opBoolean","COPY",FACE,{"derivedFrom":makeQuery(id+"F4.opExtrude","SWEPT_FACE",FACE,{"disambiguationData":[OSD([sQuery(id+"F3.wireOp",EDGE,"E17.2.1")])]})});
            chamfer(context, id + "F6", {"entities" : qUnion([Q0]), "width" : 1 * mm, "tangentPropagation" : true});
        }
    });
